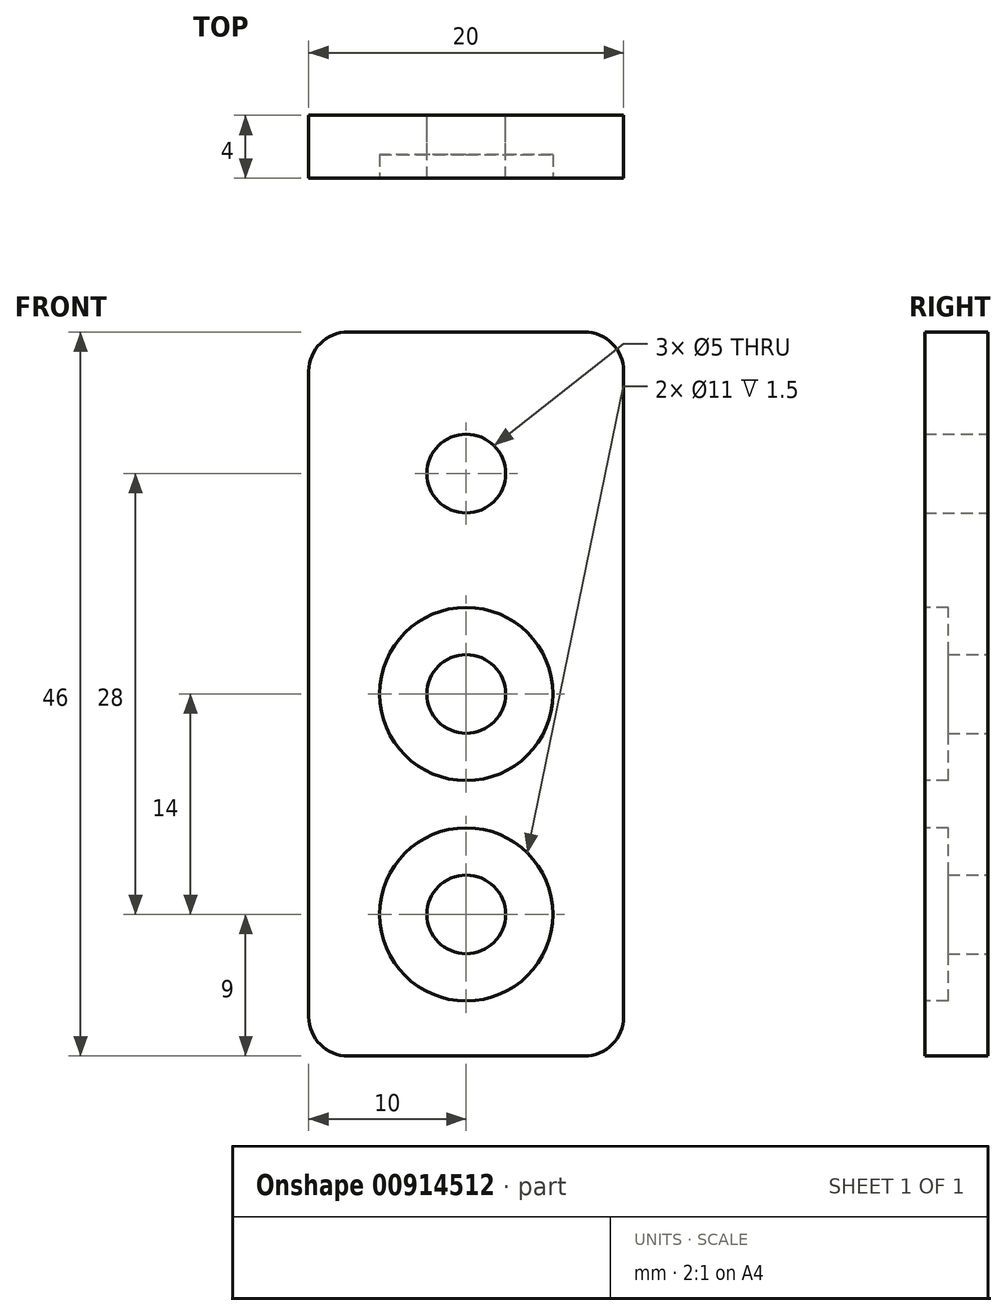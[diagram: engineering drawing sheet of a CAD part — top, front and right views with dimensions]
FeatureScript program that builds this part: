
annotation { "Feature Type Name" : "Feature", "Feature Type Description" : "" }
export const myFeature = defineFeature(function(context is Context, id is Id, definition is map)
    precondition{}
    {
        {
            var Q0;
            Q0=qCreatedBy(makeId("Front.planeOp"),FACE);
            var sketch = newSketch(context, id + "F0", { "sketchPlane" : qUnion([Q0])});
            skLineSegment(sketch, "E0.bottom", {"start": v(10, 23) * mm, "end": v(-10, 23) * mm});
            skLineSegment(sketch, "E0.top", {"start": v(10, -23) * mm, "end": v(-10, -23) * mm});
            skLineSegment(sketch, "E0.left", {"start": v(10, 23) * mm, "end": v(10, -23) * mm});
            skLineSegment(sketch, "E0.right", {"start": v(-10, 23) * mm, "end": v(-10, -23) * mm});
            skPoint(sketch, "E0.middle", {"position": v(0, 0) * mm});
            skPoint(sketch, "E1", {"position": v(0, 14) * mm});
            skPoint(sketch, "E2", {"position": v(0, -14) * mm});
            skSolve(sketch);
        }
        {
            var Q0;
            Q0=qSketchRegion(id+"F0",true);
            extrude(context, id + "F1", {"entities" : qUnion([Q0]), "depth" : 4 * mm, "offsetDistance" : 25 * mm});
        }
        {
            var Q0;
            Q0=sQuery(id+"F0.wireOp",VERTEX,"E1");
            var Q1;
            Q1=sQuery(id+"F0.wireOp",VERTEX,"E0.middle");
            var Q2;
            Q2=sQuery(id+"F0.wireOp",VERTEX,"E2");
            var Q3;
            Q3=makeQuery(id+"F1.opExtrude","SWEPT_BODY",BODY,{"disambiguationData":[OSD([sQuery(id+"F0.wireOp",EDGE,"E0.bottom"),sQuery(id+"F0.wireOp",EDGE,"E0.top"),sQuery(id+"F0.wireOp",EDGE,"E0.left"),sQuery(id+"F0.wireOp",EDGE,"E0.right")])]});
            hole(context, id + "F2", {"style" : HoleStyle.SIMPLE, "endStyle" : HoleEndStyle.THROUGH, "oppositeDirection" : true, "holeDiameter" : 5 * mm, "majorDiameter" : 5 * mm, "isTappedThrough" : true, "tappedDepth" : 12 * mm, "tapClearance" : 3, "locations" : qUnion([Q0, Q1, Q2]), "scope" : qUnion([Q3])});
        }
        {
            var Q0;
            Q0=makeQuery(id+"F1.opExtrude","CAP_FACE",FACE,{"disambiguationData":[OSD([sQuery(id+"F0.wireOp",EDGE,"E0.bottom"),sQuery(id+"F0.wireOp",EDGE,"E0.top"),sQuery(id+"F0.wireOp",EDGE,"E0.left"),sQuery(id+"F0.wireOp",EDGE,"E0.right")])],"isStart":false});
            var sketch = newSketch(context, id + "F3", { "sketchPlane" : qUnion([Q0])});
            skCircle(sketch, "E3", {"center": v(0, 0) * mm, "radius": 5.5 * mm});
            skCircle(sketch, "E4", {"center": v(0, -14) * mm, "radius": 5.5 * mm});
            skSolve(sketch);
        }
        {
            var Q0;
            Q0=qSketchRegion(id+"F3",true);
            extrude(context, id + "F4", {"entities" : qUnion([Q0]), "operationType" : NewBodyOperationType.REMOVE, "oppositeDirection" : true, "depth" : 1.5 * mm, "offsetDistance" : 25 * mm});
        }
        {
            var Q0;
            Q0=makeQuery(id+"F1.opExtrude","SWEPT_EDGE",EDGE,{"disambiguationData":[OSD([sQuery(id+"F0.wireOp",EDGE,"E0.bottom"),sQuery(id+"F0.wireOp",EDGE,"E0.left")])]});
            var Q1;
            Q1=makeQuery(id+"F1.opExtrude","SWEPT_EDGE",EDGE,{"disambiguationData":[OSD([sQuery(id+"F0.wireOp",EDGE,"E0.bottom"),sQuery(id+"F0.wireOp",EDGE,"E0.right")])]});
            var Q2;
            Q2=makeQuery(id+"F1.opExtrude","SWEPT_EDGE",EDGE,{"disambiguationData":[OSD([sQuery(id+"F0.wireOp",EDGE,"E0.top"),sQuery(id+"F0.wireOp",EDGE,"E0.left")])]});
            var Q3;
            Q3=makeQuery(id+"F1.opExtrude","SWEPT_EDGE",EDGE,{"disambiguationData":[OSD([sQuery(id+"F0.wireOp",EDGE,"E0.top"),sQuery(id+"F0.wireOp",EDGE,"E0.right")])]});
            fillet(context, id + "F5", {"entities" : qUnion([Q0, Q1, Q2, Q3]), "radius" : 2.5 * mm, "tangentPropagation" : true, "allowEdgeOverflow" : false});
        }
    });
